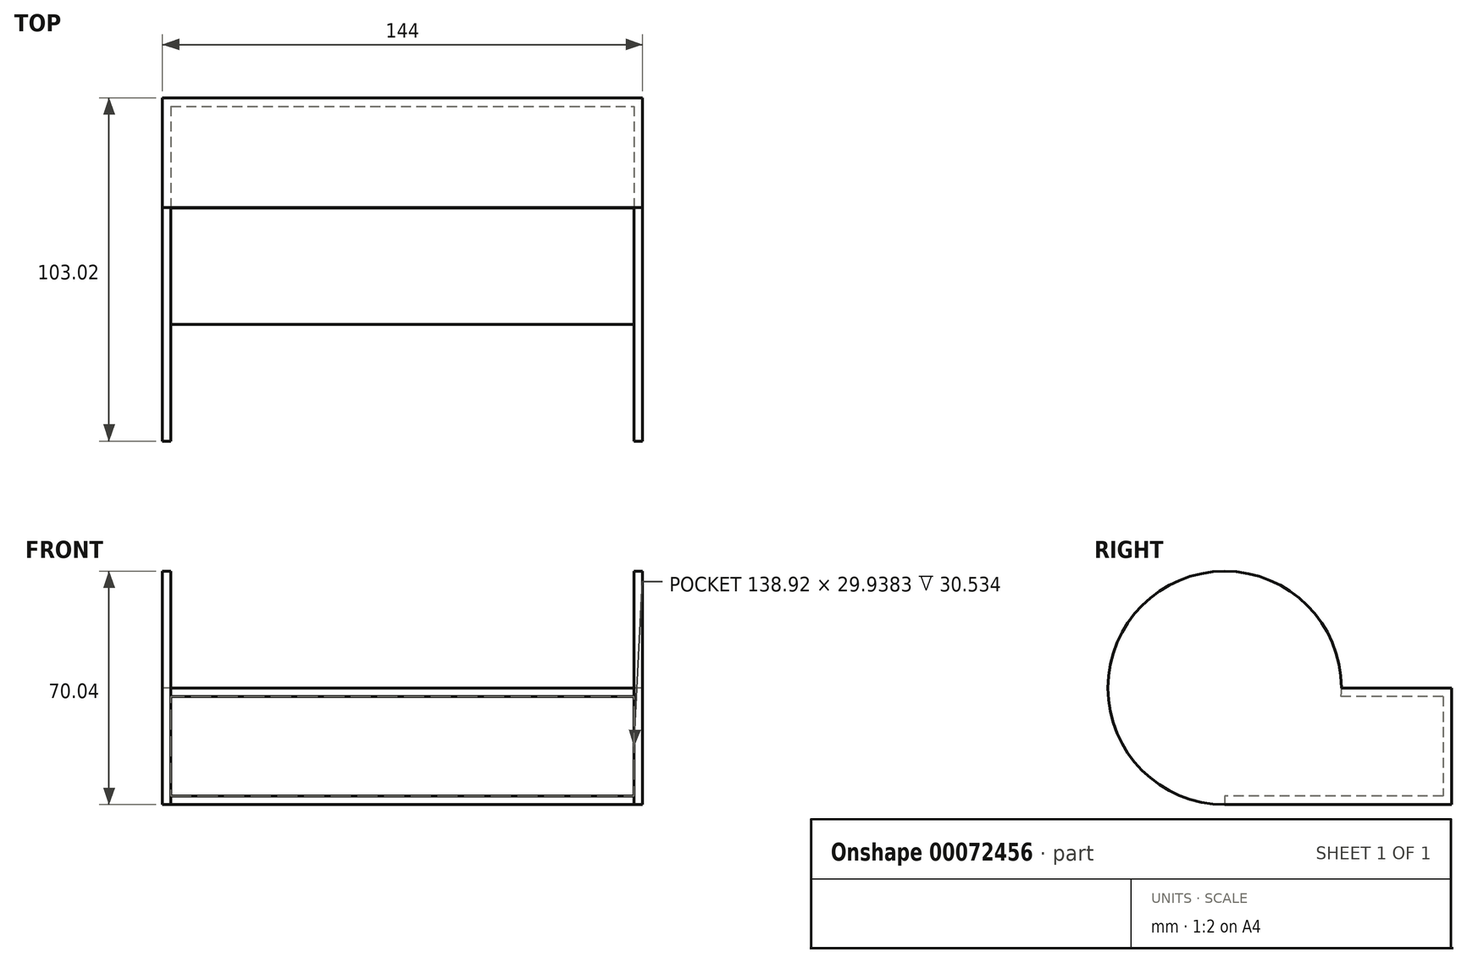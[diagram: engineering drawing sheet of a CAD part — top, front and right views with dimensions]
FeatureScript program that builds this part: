
annotation { "Feature Type Name" : "Feature", "Feature Type Description" : "" }
export const myFeature = defineFeature(function(context is Context, id is Id, definition is map)
    precondition{}
    {
        {
            var Q0;
            Q0=qCreatedBy(makeId("Top.planeOp"),FACE);
            var sketch = newSketch(context, id + "F0", { "sketchPlane" : qUnion([Q0])});
            skLineSegment(sketch, "E0.bottom", {"start": v(-72, 34) * mm, "end": v(72, 34) * mm});
            skLineSegment(sketch, "E0.top", {"start": v(-72, -34) * mm, "end": v(72, -34) * mm});
            skLineSegment(sketch, "E0.left", {"start": v(-72, 34) * mm, "end": v(-72, -34) * mm});
            skLineSegment(sketch, "E0.right", {"start": v(72, 34) * mm, "end": v(72, -34) * mm});
            skSolve(sketch);
        }
        {
            var Q0;
            Q0=makeQuery(id+"F0.imprint","IMPRINT",FACE,{"disambiguationData":[TD([[makeQuery(id+"F0.imprint","IMPRINT",EDGE,{"derivedFrom":sQuery(id+"F0.wireOp",EDGE,"E0.bottom")}),-1.0]])]});
            extrude(context, id + "F1", {"entities" : qUnion([Q0]), "depth" : 2 * mm});
        }
        {
            var Q0;
            Q0=makeQuery(id+"F1.opExtrude","CAP_FACE",FACE,{"disambiguationData":[OSD([sQuery(id+"F0.wireOp",EDGE,"E0.bottom"),sQuery(id+"F0.wireOp",EDGE,"E0.top"),sQuery(id+"F0.wireOp",EDGE,"E0.left"),sQuery(id+"F0.wireOp",EDGE,"E0.right")])],"isStart":false});
            extrude(context, id + "F2", {"entities" : qUnion([Q0]), "operationType" : NewBodyOperationType.ADD, "depth" : 33.02 * mm});
        }
        {
            var Q0;
            {var subQ0=sQuery(id+"F0.wireOp",EDGE,"E0.top");Q0=makeQuery(id+"F2.boolean.opBoolean","MERGE",FACE,{"derivedFrom":[makeQuery(id+"F1.opExtrude","SWEPT_FACE",FACE,{"disambiguationData":[OSD([subQ0])]}),makeQuery(id+"F2.opExtrude","SWEPT_FACE",FACE,{"disambiguationData":[OSD([subQ0])]})]});}
            var Q1;
            Q1=makeQuery(id+"F2.opExtrude","CAP_EDGE",EDGE,{"disambiguationData":[OSD([sQuery(id+"F0.wireOp",EDGE,"E0.top")])],"isStart":false});
            revolve(context, id + "F3", {"operationType" : NewBodyOperationType.ADD, "entities" : qUnion([Q0]), "axis" : qUnion([Q1]), "revolveType" : RevolveType.FULL});
        }
        {
            var Q0;
            Q0=makeQuery(id+"F3.opRevolve","SWEPT_FACE",FACE,{"disambiguationData":[OSD([sQuery(id+"F0.wireOp",EDGE,"E0.top")])]});
            shell(context, id + "F4", {"entities" : qUnion([Q0]), "thickness" : 2.54 * mm});
        }
    });
